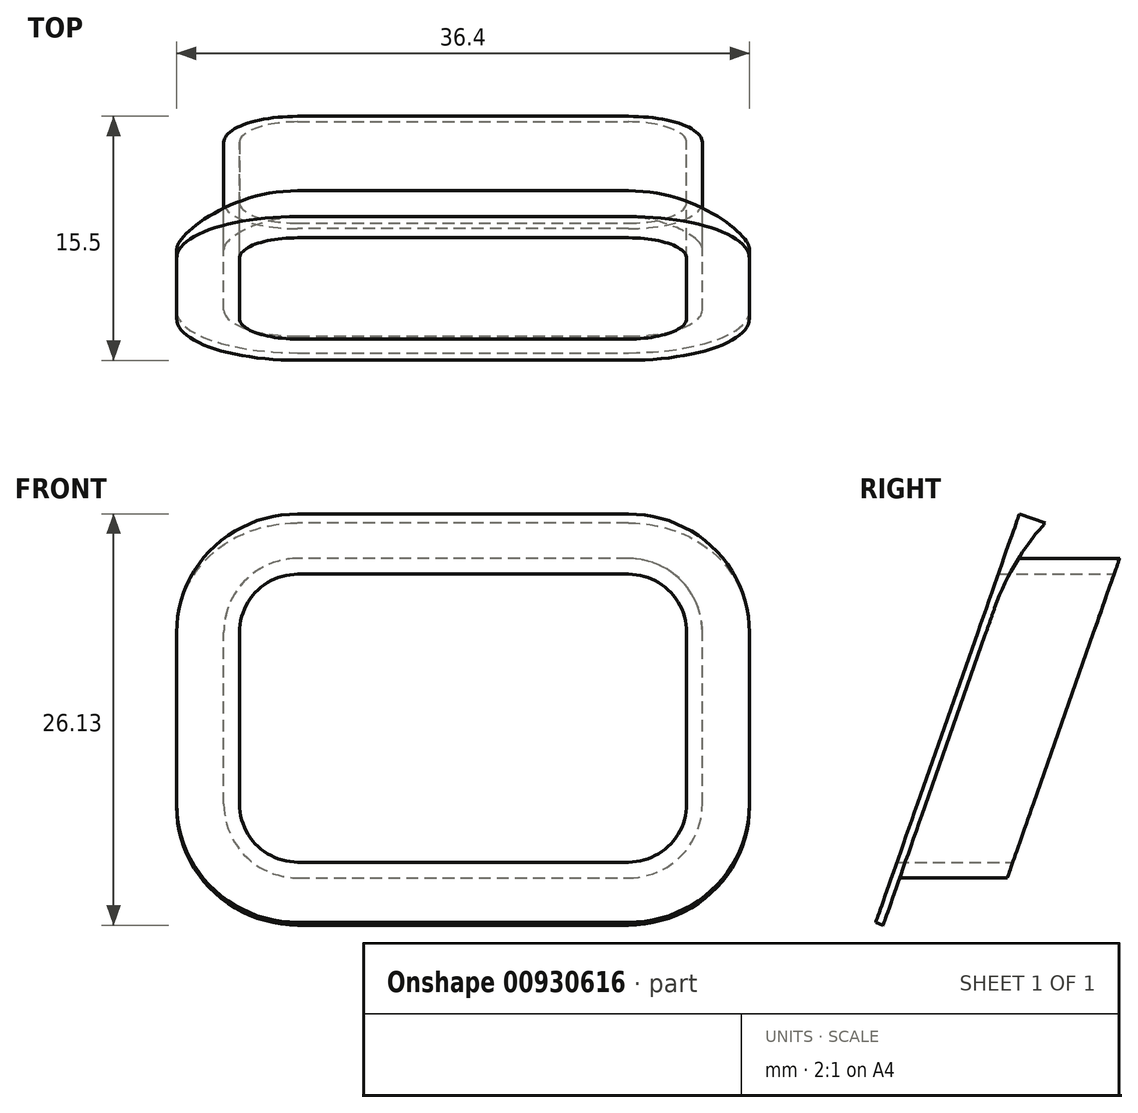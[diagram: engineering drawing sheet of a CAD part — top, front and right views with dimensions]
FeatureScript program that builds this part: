
annotation { "Feature Type Name" : "Feature", "Feature Type Description" : "" }
export const myFeature = defineFeature(function(context is Context, id is Id, definition is map)
    precondition{}
    {
        {
            var Q0;
            Q0=qCreatedBy(makeId("Front.planeOp"),FACE);
            var sketch = newSketch(context, id + "F0", { "sketchPlane" : qUnion([Q0])});
            skLineSegment(sketch, "E0.top", {"start": v(-5, 20.9) * mm, "end": v(-26, 20.9) * mm, "construction": true});
            skLineSegment(sketch, "E0.left", {"start": v(0, 5) * mm, "end": v(0, 15.9) * mm, "construction": true});
            skLineSegment(sketch, "E0.right", {"start": v(-31, 5) * mm, "end": v(-31, 15.9) * mm, "construction": true});
            skLineSegment(sketch, "E1.top", {"start": v(-26, 20.6) * mm, "end": v(-5, 20.6) * mm});
            skLineSegment(sketch, "E1.left", {"start": v(-30.7, 5) * mm, "end": v(-30.7, 15.9) * mm});
            skLineSegment(sketch, "E1.right", {"start": v(-0.3, 5) * mm, "end": v(-0.3, 15.9) * mm});
            skLineSegment(sketch, "E2", {"start": v(-29.7, 15.9) * mm, "end": v(-29.7, 5) * mm});
            skLineSegment(sketch, "E3", {"start": v(-1.3, 5) * mm, "end": v(-1.3, 15.9) * mm});
            skLineSegment(sketch, "E4", {"start": v(-26, 19.6) * mm, "end": v(-5, 19.6) * mm});
            skLineSegment(sketch, "E5", {"start": v(-26, 0) * mm, "end": v(-5, 0) * mm, "construction": true});
            skPoint(sketch, "E6.visualSharp", {"position": v(-31, 0) * mm});
            skArc(sketch, "E6.filletArc", {"start": v(-31, 5) * mm, "mid": v(-29.54, 1.46) * mm, "end": v(-26, 0) * mm, "construction": true});
            skPoint(sketch, "E7.visualSharp", {"position": v(-31, 20.9) * mm});
            skArc(sketch, "E7.filletArc", {"start": v(-26, 20.9) * mm, "mid": v(-29.54, 19.44) * mm, "end": v(-31, 15.9) * mm, "construction": true});
            skPoint(sketch, "E8.visualSharp", {"position": v(0, 20.9) * mm});
            skArc(sketch, "E8.filletArc", {"start": v(0, 15.9) * mm, "mid": v(-1.46, 19.44) * mm, "end": v(-5, 20.9) * mm, "construction": true});
            skPoint(sketch, "E9.visualSharp", {"position": v(0, 0) * mm});
            skArc(sketch, "E9.filletArc", {"start": v(-5, 0) * mm, "mid": v(-1.46, 1.46) * mm, "end": v(0, 5) * mm, "construction": true});
            skArc(sketch, "E10", {"start": v(-26, 20.6) * mm, "mid": v(-29.32, 19.22) * mm, "end": v(-30.7, 15.9) * mm});
            skLineSegment(sketch, "E11", {"start": v(-26, 1.3) * mm, "end": v(-5, 1.3) * mm});
            skLineSegment(sketch, "E12", {"start": v(-26, 0.3) * mm, "end": v(-5, 0.3) * mm});
            skArc(sketch, "E13", {"start": v(-26, 19.6) * mm, "mid": v(-28.62, 18.52) * mm, "end": v(-29.7, 15.9) * mm});
            skArc(sketch, "E14", {"start": v(-0.3, 15.9) * mm, "mid": v(-1.68, 19.22) * mm, "end": v(-5, 20.6) * mm});
            skArc(sketch, "E15", {"start": v(-29.7, 5) * mm, "mid": v(-28.62, 2.38) * mm, "end": v(-26, 1.3) * mm});
            skArc(sketch, "E16", {"start": v(-5, 1.3) * mm, "mid": v(-2.38, 2.38) * mm, "end": v(-1.3, 5) * mm});
            skArc(sketch, "E17", {"start": v(-5, 0.3) * mm, "mid": v(-1.68, 1.68) * mm, "end": v(-0.3, 5) * mm});
            skArc(sketch, "E18", {"start": v(-30.7, 5) * mm, "mid": v(-29.32, 1.68) * mm, "end": v(-26, 0.3) * mm});
            skArc(sketch, "E19", {"start": v(-1.3, 15.9) * mm, "mid": v(-2.38, 18.52) * mm, "end": v(-5, 19.6) * mm});
            skSolve(sketch);
        }
        {
            var Q0;
            Q0=qSketchRegion(id+"F0",true);
            extrude(context, id + "F1", {"entities" : qUnion([Q0]), "depth" : 14.5 * mm, "offsetDistance" : 25 * mm});
        }
        {
            var Q0;
            Q0=makeQuery(id+"F1.opExtrude","SWEPT_FACE",FACE,{"disambiguationData":[OSD([sQuery(id+"F0.wireOp",EDGE,"E1.left")])]});
            var sketch = newSketch(context, id + "F2", { "sketchPlane" : qUnion([Q0])});
            skLineSegment(sketch, "E20", {"start": v(7.36, 20.6) * mm, "end": v(14.5, 0.3) * mm});
            skLineSegment(sketch, "E21", {"start": v(14.5, 0.3) * mm, "end": v(14.5, 20.6) * mm});
            skLineSegment(sketch, "E22", {"start": v(14.5, 20.6) * mm, "end": v(7.36, 20.6) * mm});
            skLineSegment(sketch, "E23", {"start": v(0, 20.6) * mm, "end": v(0, 0.3) * mm});
            skLineSegment(sketch, "E24", {"start": v(0, 0.3) * mm, "end": v(7.14, 0.3) * mm});
            skLineSegment(sketch, "E25", {"start": v(7.14, 0.3) * mm, "end": v(0, 20.6) * mm});
            skSolve(sketch);
        }
        {
            var Q0;
            Q0=qSketchRegion(id+"F2",true);
            var Q1;
            Q1=makeQuery(id+"F1.opExtrude","SWEPT_FACE",FACE,{"disambiguationData":[OSD([sQuery(id+"F0.wireOp",EDGE,"E1.right")])]});
            extrude(context, id + "F3", {"entities" : qUnion([Q0]), "operationType" : NewBodyOperationType.REMOVE, "endBound" : BoundingType.UP_TO_SURFACE, "oppositeDirection" : true, "depth" : 25 * mm, "endBoundEntityFace" : qUnion([Q1]), "offsetDistance" : 25 * mm});
        }
        {
            var Q0;
            Q0=makeQuery(id+"F3.boolean.opBoolean","COPY",FACE,{"derivedFrom":makeQuery(id+"F3.opExtrude","SWEPT_FACE",FACE,{"disambiguationData":[OSD([sQuery(id+"F2.wireOp",EDGE,"E20")])]})});
            var sketch = newSketch(context, id + "F4", { "sketchPlane" : qUnion([Q0])});
            skEllipticalArc(sketch, "E26", {});
            skEllipticalArc(sketch, "E27", {});
            skLineSegment(sketch, "E28", {"start": v(-26, 17) * mm, "end": v(-5, 17) * mm});
            skLineSegment(sketch, "E29", {"start": v(-30.7, 12) * mm, "end": v(-30.7, 0.46) * mm, "construction": true});
            skEllipticalArc(sketch, "E30", {});
            skEllipticalArc(sketch, "E31", {});
            skLineSegment(sketch, "E32", {"start": v(-26, 20) * mm, "end": v(-5, 20) * mm});
            skLineSegment(sketch, "E33", {"start": v(-33.7, 12) * mm, "end": v(-33.7, 0.46) * mm});
            skLineSegment(sketch, "E34", {"start": v(-30.7, 0.46) * mm, "end": v(-30.3, 0.46) * mm, "construction": true});
            skEllipticalArc(sketch, "E35", {});
            skLineSegment(sketch, "E36", {"start": v(-26, -7.53) * mm, "end": v(-5, -7.53) * mm});
            skLineSegment(sketch, "E37", {"start": v(-26, -4.13) * mm, "end": v(-5, -4.13) * mm});
            skEllipticalArc(sketch, "E38", {});
            skPoint(sketch, "E39.end.orphan", {"position": v(-26, -3.47) * mm});
            skLineSegment(sketch, "E40", {"start": v(-30.7, 0.46) * mm, "end": v(-33.7, 0.46) * mm, "construction": true});
            skLineSegment(sketch, "E41", {"start": v(-5, -4.53) * mm, "end": v(-5, -7.53) * mm, "construction": true});
            skLineSegment(sketch, "E42", {"start": v(-0.3, 12) * mm, "end": v(-0.3, 0.46) * mm, "construction": true});
            skLineSegment(sketch, "E43", {"start": v(-0.3, 0.46) * mm, "end": v(-0.7, 0.46) * mm, "construction": true});
            skEllipticalArc(sketch, "E44", {});
            skLineSegment(sketch, "E45", {"start": v(-0.7, 0.46) * mm, "end": v(-0.7, 14.02) * mm, "construction": true});
            skLineSegment(sketch, "E46", {"start": v(-5, -4.53) * mm, "end": v(-5, -4.13) * mm, "construction": true});
            skLineSegment(sketch, "E47", {"start": v(2.7, 12) * mm, "end": v(2.7, 0.46) * mm});
            skEllipticalArc(sketch, "E48", {});
            skLineSegment(sketch, "E49", {"start": v(-30.7, 12) * mm, "end": v(-30.3, 0.46) * mm});
            skLineSegment(sketch, "E50", {"start": v(-0.3, 12) * mm, "end": v(-0.7, 0.46) * mm});
            const initialGuessF4  = {"E26": [-0.026, 0.012009516246810716, 0, 1, 0.004982070124227617, 0.0047, 0, 1.5707963267948968], "E27": [-0.005, 0.012009516246810669, 0, 1, 0.004982070124227669, 0.0047, 4.71238898038469, 0], "E30": [-0.026, 0.012009516246810716, 0, 1, 0.00798207012422766, 0.0077, 0, 1.5707963267948966], "E31": [-0.005, 0.012009516246810669, 0, 1, 0.007982070124227665, 0.0077, 4.71238898038469, 0], "E35": [-0.026, 0.000455353618282688, -1, 0, 0.0077, 0.00798207012422767, 6.283185307179586, 1.5707963267948966], "E38": [-0.026, 0.0004553536182826884, 0, -1, 0.00458207012422767, 0.0043, 4.71238898038469, 0], "E44": [-0.005, 0.000455353618282688, 0, -1, 0.004582070124227671, 0.0043, 0, 1.5707963267948966], "E48": [-0.005, 0.000455353618282688, 1, 0, 0.0077, 0.00798207012422767, 4.71238898038469, 6.283185307179586]};
            skSetInitialGuess(sketch, initialGuessF4);
            skSolve(sketch);
        }
        {
            var Q0;
            Q0=qSketchRegion(id+"F4",true);
            extrude(context, id + "F5", {"entities" : qUnion([Q0]), "operationType" : NewBodyOperationType.ADD, "oppositeDirection" : true, "depth" : 0.5 * mm, "offsetDistance" : 25 * mm});
        }
        {
            var Q0;
            Q0=makeQuery(id+"F5.opExtrude","SWEPT_FACE",FACE,{"disambiguationData":[OSD([sQuery(id+"F4.wireOp",EDGE,"E33")])]});
            var sketch = newSketch(context, id + "F6", { "sketchPlane" : qUnion([Q0])});
            skLineSegment(sketch, "E51", {"start": v(5.9, 23.26) * mm, "end": v(4.73, 22.85) * mm});
            skLineSegment(sketch, "E52", {"start": v(7.94, 17.44) * mm, "end": v(5.9, 23.26) * mm});
            skArc(sketch, "E53", {"start": v(7.94, 17.44) * mm, "mid": v(6.6, 20.3) * mm, "end": v(4.73, 22.85) * mm});
            skSolve(sketch);
        }
        {
            var Q0;
            Q0=qSketchRegion(id+"F6",true);
            var Q1;
            Q1=makeQuery(id+"F5.opExtrude","SWEPT_FACE",FACE,{"disambiguationData":[OSD([sQuery(id+"F4.wireOp",EDGE,"E47")])]});
            extrude(context, id + "F7", {"entities" : qUnion([Q0]), "operationType" : NewBodyOperationType.ADD, "endBound" : BoundingType.UP_TO_SURFACE, "oppositeDirection" : true, "depth" : 25 * mm, "endBoundEntityFace" : qUnion([Q1]), "offsetDistance" : 25 * mm});
        }
        {
            var Q0;
            {var subQ1=sQuery(id+"F4.wireOp",EDGE,"E31");var subQ4=sQuery(id+"F6.wireOp",EDGE,"E52");Q0=makeQuery(id+"F7.boolean.opBoolean","SPLIT",FACE,{"disambiguationData":[TD([makeQuery(id+"F5.opExtrude","SWEPT_FACE",FACE,{"disambiguationData":[OSD([subQ1])]})])],"derivedFrom":makeQuery(id+"F7.opExtrude","SWEPT_FACE",FACE,{"disambiguationData":[OSD([subQ4])]})});}
            var sketch = newSketch(context, id + "F8", { "sketchPlane" : qUnion([Q0])});
            skLineSegment(sketch, "E54", {"start": v(-33.7, 20) * mm, "end": v(-33.7, 13.81) * mm});
            skLineSegment(sketch, "E55", {"start": v(-33.7, 13.81) * mm, "end": v(-33.5, 13.81) * mm});
            skLineSegment(sketch, "E56", {"start": v(-33.7, 20) * mm, "end": v(-26, 20) * mm});
            skEllipticalArc(sketch, "E57", {});
            skEllipticalArc(sketch, "E58", {});
            skLineSegment(sketch, "E59", {"start": v(-5, 20) * mm, "end": v(2.7, 20) * mm});
            skLineSegment(sketch, "E60", {"start": v(2.7, 20) * mm, "end": v(2.7, 13.81) * mm});
            skLineSegment(sketch, "E61", {"start": v(2.7, 13.81) * mm, "end": v(2.5, 13.81) * mm});
            const initialGuessF8  = {"E57": [-0.026, 0.012009516246810716, 0, 1, 0.00798207012422766, 0.0077, 0, 1.3426863747909963], "E58": [-0.005, 0.012009516246810667, 0, 1, 0.007982070124227665, 0.0077, 4.940498932388157, 0]};
            skSetInitialGuess(sketch, initialGuessF8);
            skSolve(sketch);
        }
        {
            var Q0;
            Q0=qSketchRegion(id+"F8",true);
            var Q1;
            {var subQ0=sQuery(id+"F6.wireOp",EDGE,"E53");Q1=makeQuery(id+"F7.boolean.opBoolean","SPLIT",FACE,{"disambiguationData":[TD([makeQuery(id+"F1.opExtrude","SWEPT_FACE",FACE,{"disambiguationData":[OSD([sQuery(id+"F0.wireOp",EDGE,"E1.top")])]})])],"derivedFrom":makeQuery(id+"F7.opExtrude","SWEPT_FACE",FACE,{"disambiguationData":[OSD([subQ0])]})});}
            extrude(context, id + "F9", {"entities" : qUnion([Q0]), "operationType" : NewBodyOperationType.REMOVE, "endBound" : BoundingType.UP_TO_SURFACE, "oppositeDirection" : true, "depth" : 25 * mm, "endBoundEntityFace" : qUnion([Q1]), "offsetDistance" : 25 * mm});
        }
        {
            var Q0;
            Q0=qCreatedBy(makeId("Front.planeOp"),FACE);
            var sketch = newSketch(context, id + "F10", { "sketchPlane" : qUnion([Q0])});
            skArc(sketch, "E62", {"start": v(-1.63, 17.44) * mm, "mid": v(-3, 19.01) * mm, "end": v(-5, 19.6) * mm});
            skArc(sketch, "E63", {"start": v(-26, 19.6) * mm, "mid": v(-28, 19.01) * mm, "end": v(-29.37, 17.44) * mm});
            skLineSegment(sketch, "E64", {"start": v(-5, 19.6) * mm, "end": v(-26, 19.6) * mm});
            skLineSegment(sketch, "E65", {"start": v(-29.37, 17.44) * mm, "end": v(-1.63, 17.44) * mm});
            skSolve(sketch);
        }
        {
            var Q0;
            Q0=qSketchRegion(id+"F10",true);
            var Q1;
            Q1=makeQuery(id+"F7.boolean.opBoolean","SPLIT",FACE,{"disambiguationData":[TD([makeQuery(id+"F1.opExtrude","SWEPT_FACE",FACE,{"disambiguationData":[OSD([sQuery(id+"F0.wireOp",EDGE,"E4")])]})])],"derivedFrom":makeQuery(id+"F7.opExtrude","SWEPT_FACE",FACE,{"disambiguationData":[OSD([sQuery(id+"F6.wireOp",EDGE,"E52")])]})});
            extrude(context, id + "F11", {"entities" : qUnion([Q0]), "operationType" : NewBodyOperationType.REMOVE, "endBound" : BoundingType.UP_TO_SURFACE, "depth" : 25 * mm, "endBoundEntityFace" : qUnion([Q1]), "offsetDistance" : 25 * mm});
        }
    });
